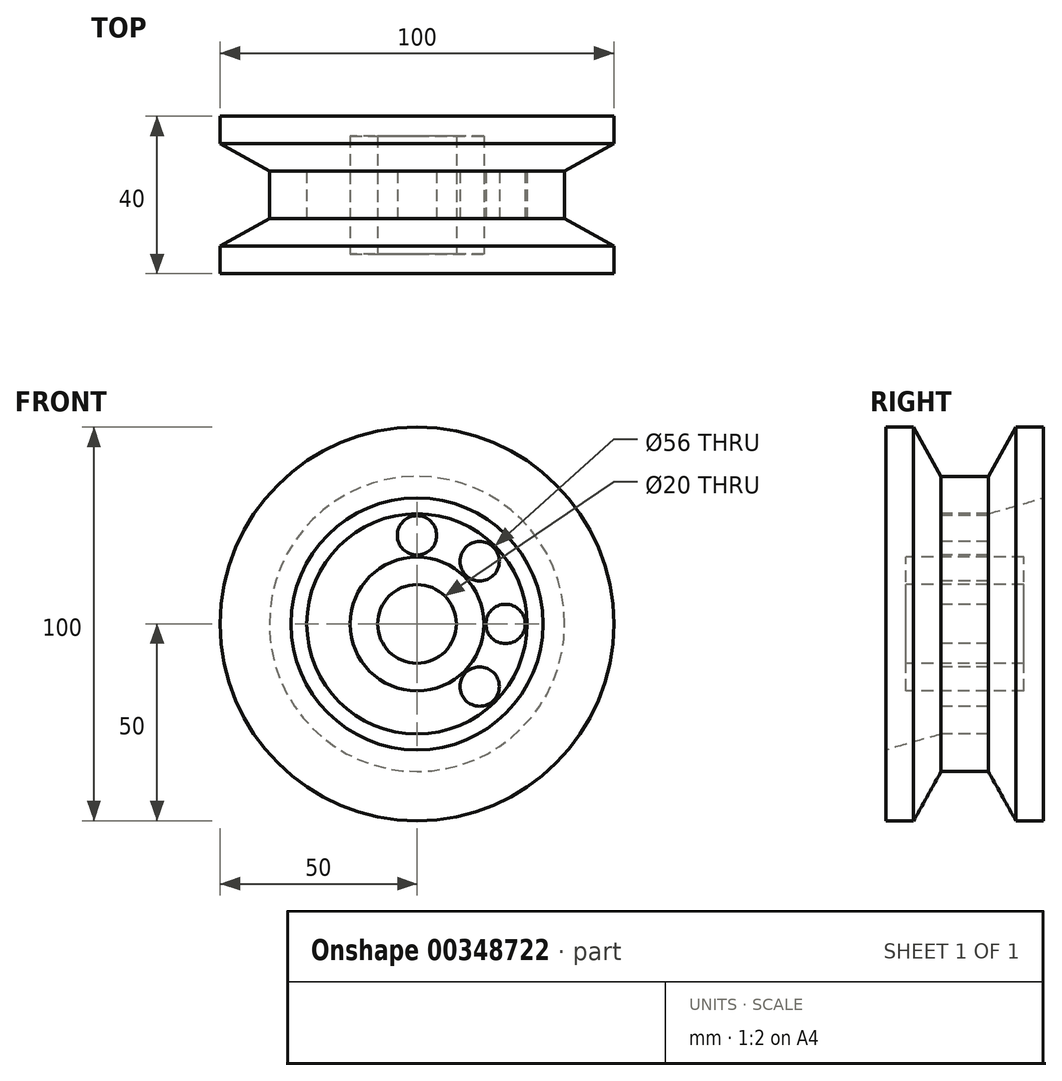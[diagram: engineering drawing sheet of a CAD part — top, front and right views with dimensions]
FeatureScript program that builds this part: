
annotation { "Feature Type Name" : "Feature", "Feature Type Description" : "" }
export const myFeature = defineFeature(function(context is Context, id is Id, definition is map)
    precondition{}
    {
        {
            var Q0;
            Q0=qCreatedBy(makeId("Right.planeOp"),FACE);
            var sketch = newSketch(context, id + "F0", { "sketchPlane" : qUnion([Q0])});
            skLineSegment(sketch, "E0", {"start": v(-20, 0) * mm, "end": v(-20, 50) * mm});
            skLineSegment(sketch, "E1", {"start": v(-6, 0) * mm, "end": v(-6, 37.5) * mm, "construction": true});
            skLineSegment(sketch, "E2", {"start": v(-6, 37.5) * mm, "end": v(-13, 50) * mm});
            skLineSegment(sketch, "E3", {"start": v(-13, 50) * mm, "end": v(-20, 50) * mm});
            skLineSegment(sketch, "E4", {"start": v(-6, 37.5) * mm, "end": v(0, 37.5) * mm});
            skLineSegment(sketch, "E5.MirrorCS", {"start": v(6, 37.5) * mm, "end": v(0, 37.5) * mm});
            skLineSegment(sketch, "E6.MirrorCS", {"start": v(6, 37.5) * mm, "end": v(13, 50) * mm});
            skLineSegment(sketch, "E7.MirrorCS", {"start": v(13, 50) * mm, "end": v(20, 50) * mm});
            skLineSegment(sketch, "E8.MirrorCS", {"start": v(20, 0) * mm, "end": v(20, 50) * mm});
            skLineSegment(sketch, "E9", {"start": v(-20, 0) * mm, "end": v(20, 0) * mm});
            skSolve(sketch);
        }
        {
            var Q0;
            Q0=makeQuery(id+"F0.imprint","IMPRINT",FACE,{"disambiguationData":[TD([[makeQuery(id+"F0.imprint","IMPRINT",EDGE,{"derivedFrom":sQuery(id+"F0.wireOp",EDGE,"E0")}),-1.0]])]});
            var Q1;
            Q1=sQuery(id+"F0.wireOp",EDGE,"E9");
            revolve(context, id + "F1", {"entities" : qUnion([Q0]), "axis" : qUnion([Q1]), "revolveType" : RevolveType.FULL});
        }
        {
            var Q0;
            Q0=makeQuery(id+"F1.opRevolve","SWEPT_FACE",FACE,{"disambiguationData":[OSD([sQuery(id+"F0.wireOp",EDGE,"E0")])]});
            var sketch = newSketch(context, id + "F2", { "sketchPlane" : qUnion([Q0])});
            skCircle(sketch, "E10", {"center": v(0, 0) * mm, "radius": 10 * mm});
            skSolve(sketch);
        }
        {
            var Q0;
            Q0=makeQuery(id+"F2.imprint","IMPRINT",FACE,{"disambiguationData":[TD([[makeQuery(id+"F2.imprint","IMPRINT",EDGE,{"derivedFrom":sQuery(id+"F2.wireOp",EDGE,"E10")}),1.0]])]});
            extrude(context, id + "F3", {"entities" : qUnion([Q0]), "operationType" : NewBodyOperationType.REMOVE, "oppositeDirection" : true, "depth" : (7 * 4 + 12) * mm});
        }
        {
            var Q0;
            Q0=qCreatedBy(makeId("Right.planeOp"),FACE);
            var sketch = newSketch(context, id + "F4", { "sketchPlane" : qUnion([Q0])});
            skLineSegment(sketch, "E11", {"start": v(0, 0) * mm, "end": v(-20, 0) * mm, "construction": true});
            skLineSegment(sketch, "E12", {"start": v(-20, -10) * mm, "end": v(-20, -32) * mm});
            skLineSegment(sketch, "E13", {"start": v(0, 0) * mm, "end": v(-15, 0) * mm, "construction": true});
            skLineSegment(sketch, "E14", {"start": v(0, 0) * mm, "end": v(-6, 0) * mm, "construction": true});
            skLineSegment(sketch, "E15", {"start": v(0, 0) * mm, "end": v(0, -17) * mm, "construction": true});
            skLineSegment(sketch, "E16", {"start": v(0, -17) * mm, "end": v(0, -28) * mm, "construction": true});
            skLineSegment(sketch, "E17", {"start": v(0, -28) * mm, "end": v(-6, -28) * mm, "construction": true});
            skLineSegment(sketch, "E18", {"start": v(-6, -28) * mm, "end": v(-20, -32) * mm});
            skLineSegment(sketch, "E19", {"start": v(-6, -17) * mm, "end": v(-6, -28) * mm});
            skLineSegment(sketch, "E20", {"start": v(-6, -17) * mm, "end": v(-15, -17) * mm});
            skLineSegment(sketch, "E21", {"start": v(-15, -17) * mm, "end": v(-15, -10) * mm});
            skLineSegment(sketch, "E22", {"start": v(0, 0) * mm, "end": v(0, -10) * mm, "construction": true});
            skLineSegment(sketch, "E23", {"start": v(-20, -10) * mm, "end": v(-15, -10) * mm});
            skLineSegment(sketch, "E24.MirrorCS", {"start": v(6, -17) * mm, "end": v(6, -28) * mm});
            skLineSegment(sketch, "E25.MirrorCS", {"start": v(6, -17) * mm, "end": v(15, -17) * mm});
            skLineSegment(sketch, "E26.MirrorCS", {"start": v(15, -17) * mm, "end": v(15, -10) * mm});
            skLineSegment(sketch, "E27.MirrorCS", {"start": v(20, -10) * mm, "end": v(15, -10) * mm});
            skLineSegment(sketch, "E28.MirrorCS", {"start": v(20, -10) * mm, "end": v(20, -32) * mm});
            skLineSegment(sketch, "E29.MirrorCS", {"start": v(6, -28) * mm, "end": v(20, -32) * mm});
            skSolve(sketch);
        }
        {
            var Q0;
            Q0 = qSketchRegion(id + "F4", true);
            var Q1;
            Q1=sQuery(id+"F4.wireOp",EDGE,"E11");
            revolve(context, id + "F5", {"operationType" : NewBodyOperationType.REMOVE, "entities" : qUnion([Q0]), "axis" : qUnion([Q1]), "revolveType" : RevolveType.FULL, "oppositeDirection" : true});
        }
        {
            var Q0;
            Q0=makeQuery(id+"F5.boolean.opBoolean","COPY",FACE,{"derivedFrom":makeQuery(id+"F5.opRevolve","SWEPT_FACE",FACE,{"disambiguationData":[OSD([sQuery(id+"F4.wireOp",EDGE,"E19")])]})});
            var sketch = newSketch(context, id + "F6", { "sketchPlane" : qUnion([Q0])});
            skLineSegment(sketch, "E30", {"start": v(0, 28) * mm, "end": v(28, 0) * mm, "construction": true});
            skLineSegment(sketch, "E31", {"start": v(28, 0) * mm, "end": v(0, -28) * mm, "construction": true});
            skLineSegment(sketch, "E32", {"start": v(0, -28) * mm, "end": v(-28, 0) * mm, "construction": true});
            skLineSegment(sketch, "E33", {"start": v(-28, 0) * mm, "end": v(0, 28) * mm, "construction": true});
            skLineSegment(sketch, "E34", {"start": v(-19.8, 19.8) * mm, "end": v(-19.8, -19.8) * mm, "construction": true});
            skLineSegment(sketch, "E35", {"start": v(-19.8, -19.8) * mm, "end": v(19.8, -19.8) * mm, "construction": true});
            skLineSegment(sketch, "E36", {"start": v(19.8, -19.8) * mm, "end": v(19.8, 19.8) * mm, "construction": true});
            skLineSegment(sketch, "E37", {"start": v(19.8, 19.8) * mm, "end": v(-19.8, 19.8) * mm, "construction": true});
            skLineSegment(sketch, "E38", {"start": v(-19.8, 19.8) * mm, "end": v(-15.9, 15.9) * mm, "construction": true});
            skCircle(sketch, "E39", {"center": v(-15.9, 15.9) * mm, "radius": 5 * mm});
            skLineSegment(sketch, "E40", {"start": v(-19.8, -19.8) * mm, "end": v(19.8, 19.8) * mm, "construction": true});
            skCircle(sketch, "E41.MirrorC", {"center": v(15.9, -15.9) * mm, "radius": 5 * mm});
            skLineSegment(sketch, "E42", {"start": v(-28, 0) * mm, "end": v(-22.5, 0) * mm, "construction": true});
            skCircle(sketch, "E43", {"center": v(-22.5, 0) * mm, "radius": 5 * mm});
            skCircle(sketch, "E44.MirrorC", {"center": v(22.5, 0) * mm, "radius": 5 * mm});
            skLineSegment(sketch, "E45", {"start": v(-19.8, -19.8) * mm, "end": v(-15.9, -15.9) * mm, "construction": true});
            skCircle(sketch, "E46", {"center": v(-15.9, -15.9) * mm, "radius": 5 * mm});
            skLineSegment(sketch, "E47", {"start": v(-15.9, 15.9) * mm, "end": v(15.9, -15.9) * mm, "construction": true});
            skCircle(sketch, "E48.MirrorC", {"center": v(15.9, 15.9) * mm, "radius": 5 * mm});
            skLineSegment(sketch, "E49", {"start": v(0, -28) * mm, "end": v(0, -22.5) * mm, "construction": true});
            skCircle(sketch, "E50", {"center": v(0, -22.5) * mm, "radius": 5 * mm});
            skCircle(sketch, "E51.MirrorC", {"center": v(0, 22.5) * mm, "radius": 5 * mm});
            skSolve(sketch);
        }
        {
            var Q0;
            Q0=makeQuery(id+"F6.imprint","IMPRINT",FACE,{"disambiguationData":[TD([[makeQuery(id+"F6.imprint","IMPRINT",EDGE,{"derivedFrom":sQuery(id+"F6.wireOp",EDGE,"E39")}),1.0]])]});
            var Q1;
            Q1=makeQuery(id+"F6.imprint","IMPRINT",FACE,{"disambiguationData":[TD([[makeQuery(id+"F6.imprint","IMPRINT",EDGE,{"derivedFrom":sQuery(id+"F6.wireOp",EDGE,"E51.MirrorC")}),-1.0]])]});
            var Q2;
            Q2=makeQuery(id+"F6.imprint","IMPRINT",FACE,{"disambiguationData":[TD([[makeQuery(id+"F6.imprint","IMPRINT",EDGE,{"derivedFrom":sQuery(id+"F6.wireOp",EDGE,"E48.MirrorC")}),-1.0]])]});
            var Q3;
            Q3=makeQuery(id+"F6.imprint","IMPRINT",FACE,{"disambiguationData":[TD([[makeQuery(id+"F6.imprint","IMPRINT",EDGE,{"derivedFrom":sQuery(id+"F6.wireOp",EDGE,"E43")}),1.0]])]});
            var Q4;
            Q4=makeQuery(id+"F6.imprint","IMPRINT",FACE,{"disambiguationData":[TD([[makeQuery(id+"F6.imprint","IMPRINT",EDGE,{"derivedFrom":sQuery(id+"F6.wireOp",EDGE,"E46")}),1.0]])]});
            var Q5;
            Q5=makeQuery(id+"F6.imprint","IMPRINT",FACE,{"disambiguationData":[TD([[makeQuery(id+"F6.imprint","IMPRINT",EDGE,{"derivedFrom":sQuery(id+"F6.wireOp",EDGE,"E50")}),1.0]])]});
            var Q6;
            Q6=makeQuery(id+"F6.imprint","IMPRINT",FACE,{"disambiguationData":[TD([[makeQuery(id+"F6.imprint","IMPRINT",EDGE,{"derivedFrom":sQuery(id+"F6.wireOp",EDGE,"E41.MirrorC")}),-1.0]])]});
            var Q7;
            Q7=makeQuery(id+"F6.imprint","IMPRINT",FACE,{"disambiguationData":[TD([[makeQuery(id+"F6.imprint","IMPRINT",EDGE,{"derivedFrom":sQuery(id+"F6.wireOp",EDGE,"E44.MirrorC")}),-1.0]])]});
            extrude(context, id + "F7", {"entities" : qUnion([Q0, Q1, Q2, Q3, Q4, Q5, Q6, Q7]), "operationType" : NewBodyOperationType.REMOVE, "oppositeDirection" : true, "depth" : 25 * mm});
        }
    });
